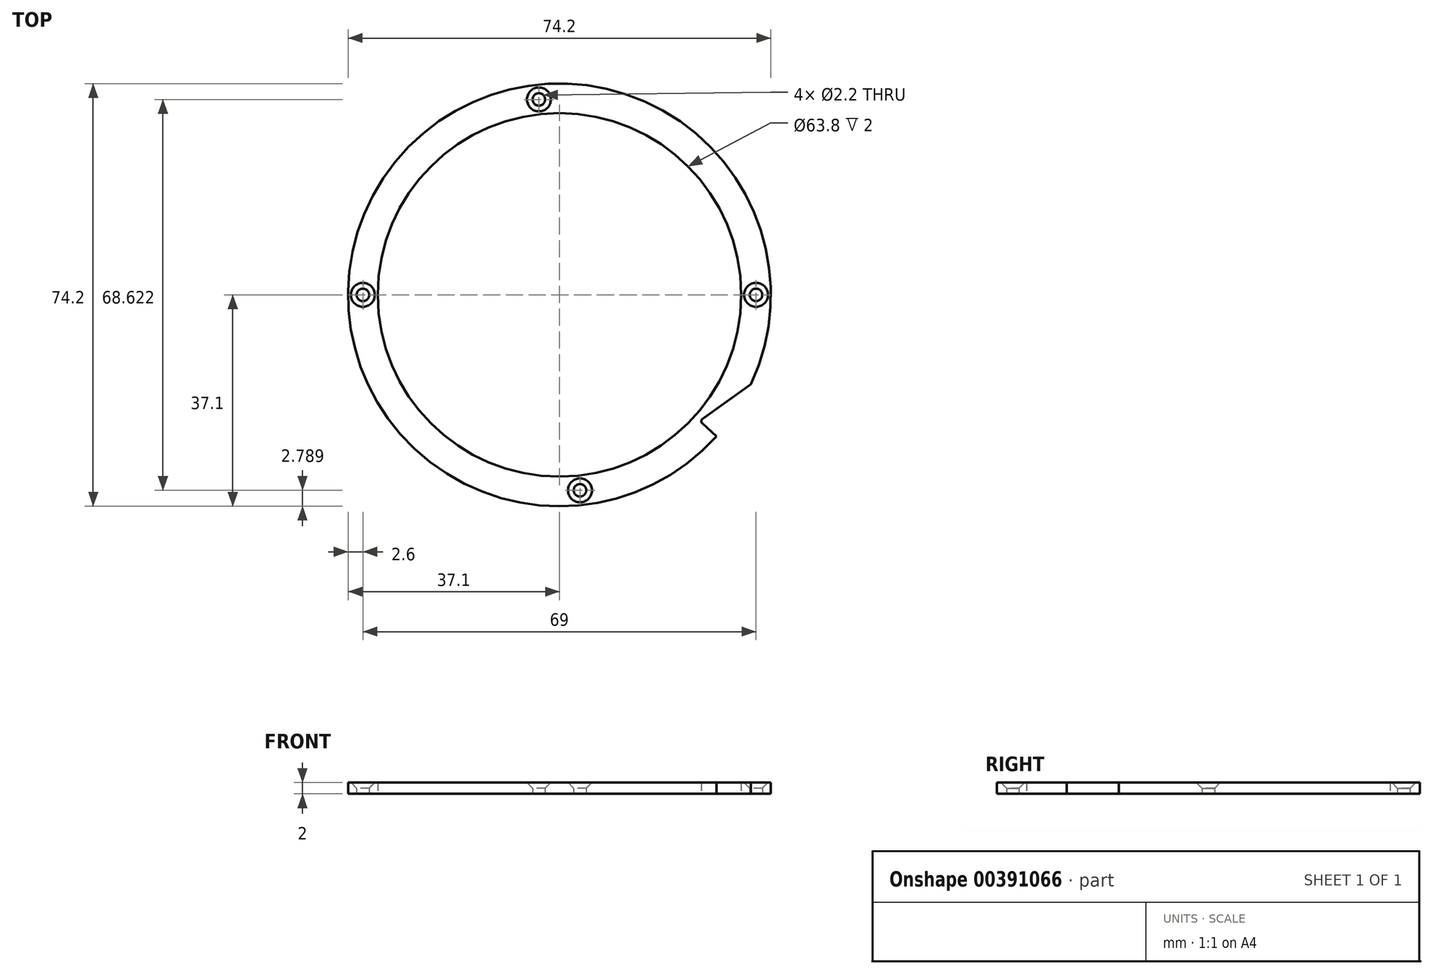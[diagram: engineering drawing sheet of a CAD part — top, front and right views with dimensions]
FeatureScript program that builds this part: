
annotation { "Feature Type Name" : "Feature", "Feature Type Description" : "" }
export const myFeature = defineFeature(function(context is Context, id is Id, definition is map)
    precondition{}
    {
        {
            var Q0;
            Q0=qCreatedBy(makeId("Top.planeOp"),FACE);
            var sketch = newSketch(context, id + "F0", { "sketchPlane" : qUnion([Q0])});
            skArc(sketch, "E0", {"start": v(33.62, -15.68) * mm, "mid": v(-30.94, 20.48) * mm, "end": v(27.57, -24.82) * mm});
            skCircle(sketch, "E1", {"center": v(0, 0) * mm, "radius": 31.9 * mm});
            skLineSegment(sketch, "E2", {"start": v(-37.1, 0) * mm, "end": v(-31.9, 0) * mm, "construction": true});
            skLineSegment(sketch, "E3.trimOffspring", {"start": v(31.9, 0) * mm, "end": v(37.1, 0) * mm, "construction": true});
            skCircle(sketch, "E4", {"center": v(0, 0) * mm, "radius": 33.1 * mm, "construction": true});
            skCircle(sketch, "E5", {"center": v(0, 0) * mm, "radius": 34.5 * mm, "construction": true});
            skLineSegment(sketch, "E6", {"start": v(0, 0) * mm, "end": v(3.88, -36.9) * mm, "construction": true});
            skCircle(sketch, "E7", {"center": v(3.6, -34.31) * mm, "radius": 1.1 * mm});
            skLineSegment(sketch, "E8", {"start": v(0, 0) * mm, "end": v(-3.88, 36.9) * mm, "construction": true});
            skCircle(sketch, "E9", {"center": v(-3.6, 34.31) * mm, "radius": 1.1 * mm});
            skCircle(sketch, "E10", {"center": v(34.5, 0) * mm, "radius": 1.1 * mm});
            skCircle(sketch, "E11", {"center": v(-34.5, 0) * mm, "radius": 1.1 * mm});
            skLineSegment(sketch, "E12", {"start": v(0, 0) * mm, "end": v(27.57, -24.82) * mm, "construction": true});
            skLineSegment(sketch, "E13", {"start": v(0, 0) * mm, "end": v(33.62, -15.68) * mm, "construction": true});
            skLineSegment(sketch, "E14", {"start": v(33.62, -15.68) * mm, "end": v(25.1, -21.79) * mm});
            skLineSegment(sketch, "E15", {"start": v(25.06, -22.56) * mm, "end": v(27.57, -24.82) * mm});
            skPoint(sketch, "E16.visualSharp", {"position": v(24.6, -22.15) * mm});
            skArc(sketch, "E16.filletArc", {"start": v(25.1, -21.79) * mm, "mid": v(24.9, -22.16) * mm, "end": v(25.06, -22.56) * mm});
            skSolve(sketch);
        }
        {
            var Q0;
            Q0=makeQuery(id+"F0.imprint","IMPRINT",FACE,{"disambiguationData":[TD([[makeQuery(id+"F0.imprint","IMPRINT",EDGE,{"derivedFrom":sQuery(id+"F0.wireOp",EDGE,"E0")}),1.0]])]});
            extrude(context, id + "F1", {"entities" : qUnion([Q0]), "depth" : 2 * mm});
        }
        {
            var Q0;
            Q0=makeQuery(id+"F1.opExtrude","CAP_EDGE",EDGE,{"disambiguationData":[OSD([sQuery(id+"F0.wireOp",EDGE,"E10")])],"isStart":false});
            var Q1;
            Q1=makeQuery(id+"F1.opExtrude","CAP_EDGE",EDGE,{"disambiguationData":[OSD([sQuery(id+"F0.wireOp",EDGE,"E9")])],"isStart":false});
            var Q2;
            Q2=makeQuery(id+"F1.opExtrude","CAP_EDGE",EDGE,{"disambiguationData":[OSD([sQuery(id+"F0.wireOp",EDGE,"E11")])],"isStart":false});
            var Q3;
            Q3=makeQuery(id+"F1.opExtrude","CAP_EDGE",EDGE,{"disambiguationData":[OSD([sQuery(id+"F0.wireOp",EDGE,"E7")])],"isStart":false});
            chamfer(context, id + "F2", {"entities" : qUnion([Q0, Q1, Q2, Q3]), "chamferType" : ChamferType.OFFSET_ANGLE, "width" : 1 * mm, "oppositeDirection" : false, "angle" : 45 * degree, "tangentPropagation" : true});
        }
    });
